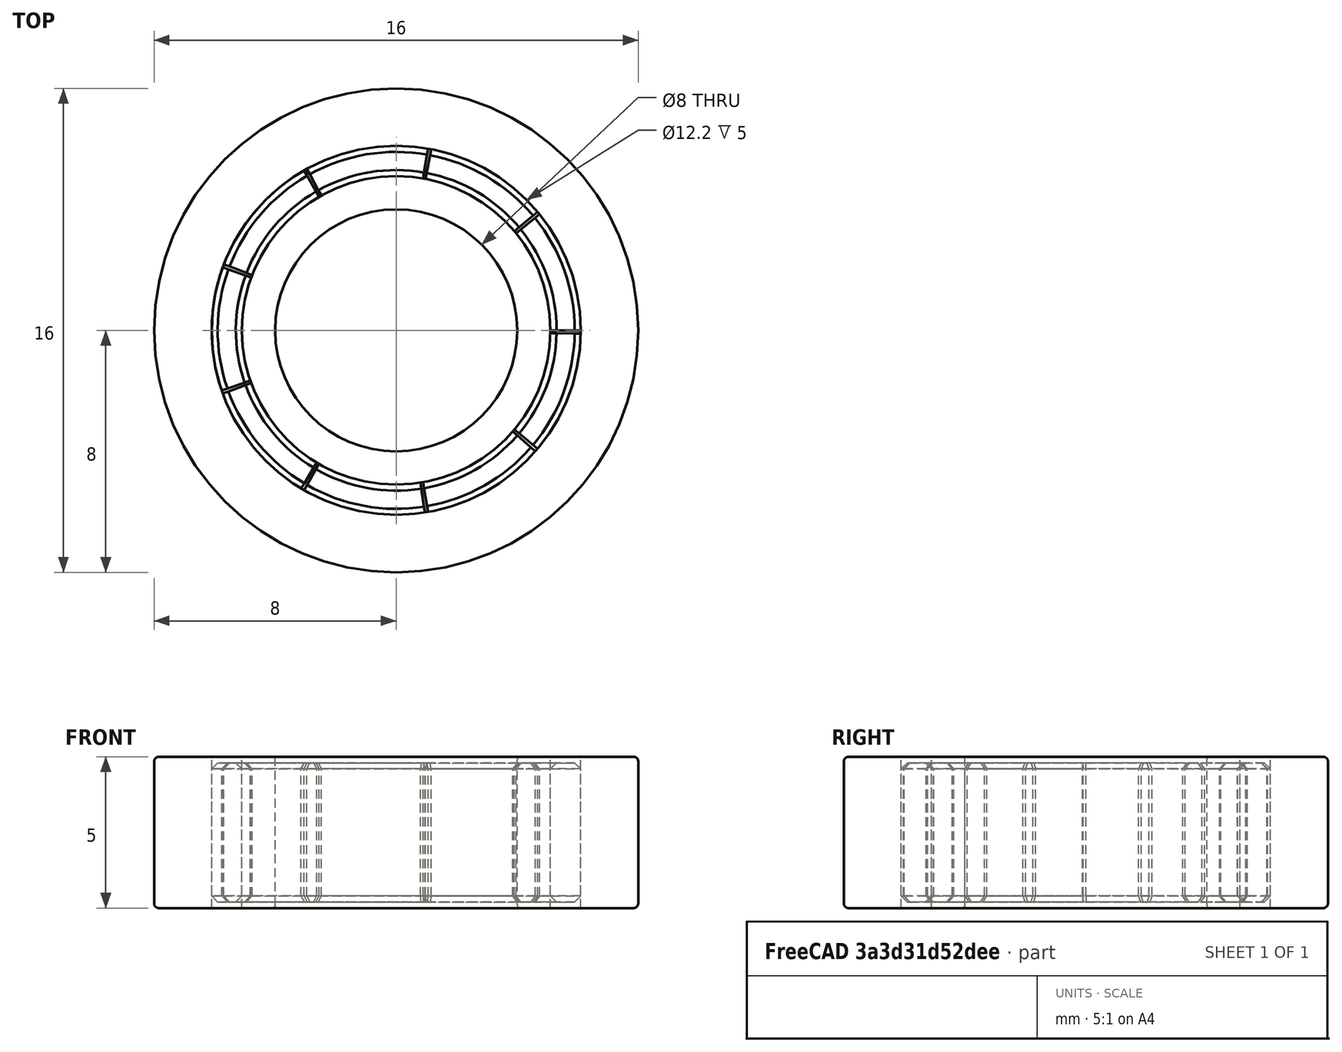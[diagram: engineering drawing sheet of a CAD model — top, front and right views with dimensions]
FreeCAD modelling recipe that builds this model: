
FCSTD DOCUMENT  (FreeCAD 0.18R16110 (Git))
Label: zz688
License: All rights reserved
LicenseURL: http://de.wikipedia.org/wiki/Alle_Rechte_vorbehalten
objects: Part::Cylinder×6, Part::Cut×3, PartDesign::Fillet×2, Part::Chamfer×1, Part::FeaturePython×1, Part::MultiFuse×1, Spreadsheet::Sheet×1, Part::Compound×1, Part::Feature×1
note: 16 computed .brp shape members not serialized (recipe doc carries the construction recipe); baked Part::Feature solids carry a one-line shape summary decoded from their .brp

FEATURE [Part::Cylinder] Cylinder  label="Exterior"
  Angle = 360
  AttacherType = Attacher::AttachEngine3D
  Height = 5
  Radius = 8
  expr: Height = Spreadsheet.Bt
  expr: Radius = Spreadsheet.De / 2
FEATURE [Part::Cylinder] Cylinder001  label="Interior"
  Angle = 360
  AttacherType = Attacher::AttachEngine3D
  Height = 5
  Radius = 4
  expr: Radius = Spreadsheet.di / 2
  expr: Height = Spreadsheet.Bt
FEATURE [Part::Cylinder] Cylinder002  label="Cilindro"
  Angle = 360
  AttacherType = Attacher::AttachEngine3D
  Height = 5
  Radius = 6.1
  expr: Height = Spreadsheet.Bt
  expr: Radius = Spreadsheet.Dm2 / 2
FEATURE [Part::Cut] Cut  label="ExtRing"
  Base = -> Cylinder
  Tool = -> Cylinder002
FEATURE [Part::Cylinder] Cylinder003  label="Cilindro001"
  Angle = 360
  AttacherType = Attacher::AttachEngine3D
  Height = 5
  Radius = 5.1
  expr: Height = Spreadsheet.Bt
  expr: Radius = Spreadsheet.Dm1 / 2
FEATURE [Part::Cut] Cut001  label="Interior001"
  Base = -> Cylinder003
  Tool = -> Cylinder001
FEATURE [Part::Cylinder] Cylinder004  label="Cilindro002"
  Angle = 39
  AttacherType = Attacher::AttachEngine3D
  Height = 4.6
  Placement = pos=(0,0,0.2) rot=(0,0,1;0rad)
  Radius = 6.1
  expr: Radius = Spreadsheet.Dm2 / 2
  expr: Height = Spreadsheet.Bt - 0.4
FEATURE [Part::Cylinder] Cylinder005  label="Cilindro003"
  Angle = 39
  AttacherType = Attacher::AttachEngine3D
  Height = 4.6
  Placement = pos=(0,0,0.2) rot=(0,0,1;0rad)
  Radius = 5.1
  expr: Height = Spreadsheet.Bt - 0.4
  expr: Radius = Spreadsheet.Dm1 / 2
FEATURE [Part::Cut] Cut002
  Base = -> Cylinder004
  Tool = -> Cylinder005
FEATURE [Part::Chamfer] Chamfer001
  Base = -> Cut002
  Edges = 4 edges r=0.2: [Edge1,Edge3,Edge6,Edge11]
FEATURE [Part::FeaturePython] Array  # Draft array (typed FeaturePython)
  Angle = 360
  ArrayType = 1
  Axis = (0,0,1)
  Base = -> Chamfer001
  Center = (0,0,0)
  IntervalX = (1,0,0)
  IntervalY = (0,1,0)
  IntervalZ = (0,0,1)
  NumberPolar = 9
  NumberX = 2
  NumberY = 2
  NumberZ = 1
FEATURE [Part::MultiFuse] Fusion  label="MidRingMetal"
  Shapes = -> [Array]
FEATURE [Spreadsheet::Sheet] Spreadsheet
  cells = B1=Principal Dimensions; C2=D; D2(De)=16; C3=d; D3(di)=8; C4=B; D4(Bt)=5; B5=Secondary Dimensions; C6=d1/d2; D6(Dm1)=10.2; C7=D2/da; D7(Dm2)=12.2; C8=r1,2; D8(rchamfer)=0.15; C9=ra; D9(ra)=0.1
FEATURE [PartDesign::Fillet] Fillet
  Base = -> Cut001 [Edge5,Edge4]
  Radius = 0.1
  expr: Radius = Spreadsheet.ra
FEATURE [PartDesign::Fillet] Fillet001
  Base = -> Cut [Edge3,Edge1]
  Radius = 0.15
  expr: Radius = Spreadsheet.rchamfer
FEATURE [Part::Compound] Compound  label="Parametric_Ball_Bearing"
  Links = -> [Fillet,Fusion,Fillet001]
FEATURE [Part::Feature] Compound001  label="Parametric_Ball_Bearing001"
  shape: bbox 17.32 x 17.32 x 5 mm, 102 faces, 11 solids (baked)
